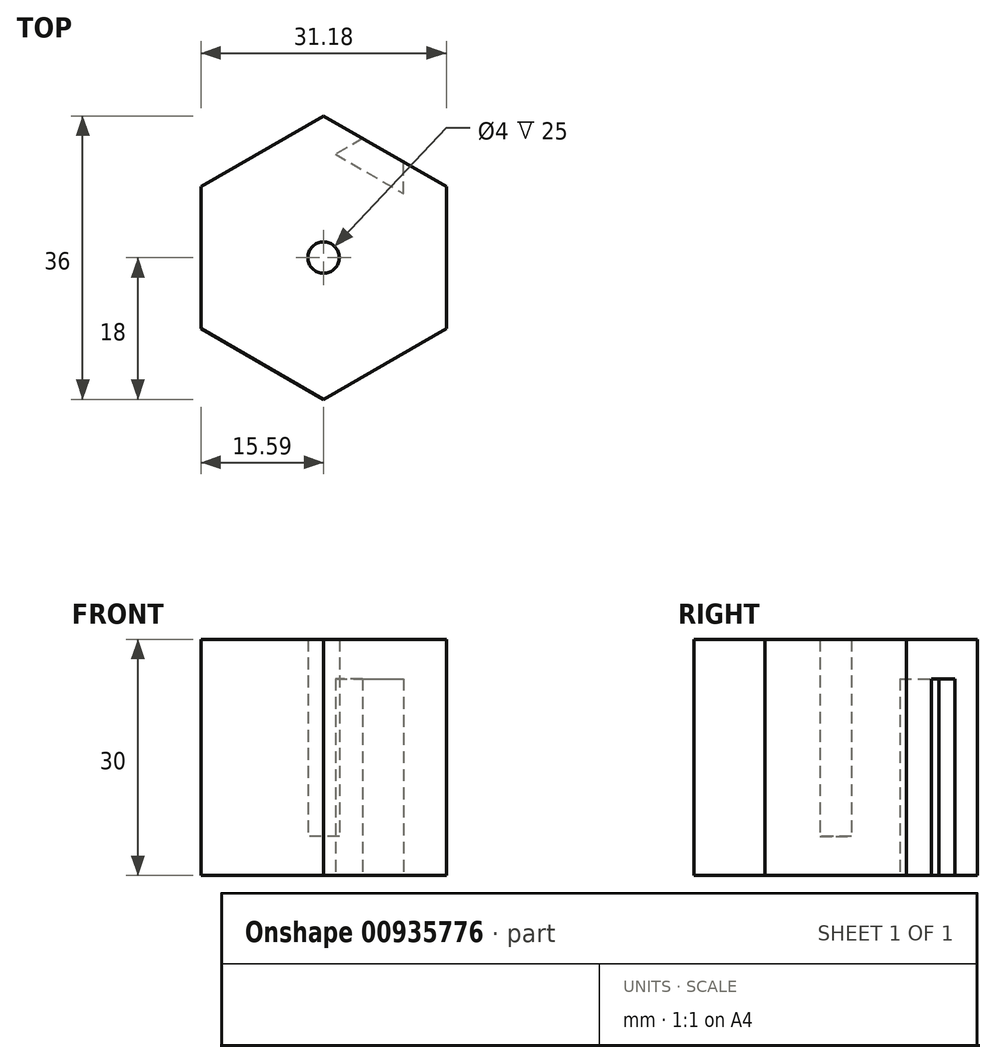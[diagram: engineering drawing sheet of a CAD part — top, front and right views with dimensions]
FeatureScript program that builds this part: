
annotation { "Feature Type Name" : "Feature", "Feature Type Description" : "" }
export const myFeature = defineFeature(function(context is Context, id is Id, definition is map)
    precondition{}
    {
        {
            var Q0;
            Q0=qCreatedBy(makeId("Top.planeOp"),FACE);
            var sketch = newSketch(context, id + "F0", { "sketchPlane" : qUnion([Q0])});
            skCircle(sketch, "E0.cCircle", {"center": v(0, 0) * mm, "radius": 18 * mm, "construction": true});
            skLineSegment(sketch, "E0.0", {"start": v(-15.59, 9) * mm, "end": v(0, 18) * mm});
            skLineSegment(sketch, "E0.1", {"start": v(0, 18) * mm, "end": v(15.59, 9) * mm});
            skLineSegment(sketch, "E0.2", {"start": v(15.59, 9) * mm, "end": v(15.59, -9) * mm});
            skLineSegment(sketch, "E0.3", {"start": v(15.59, -9) * mm, "end": v(0, -18) * mm});
            skLineSegment(sketch, "E0.4", {"start": v(0, -18) * mm, "end": v(-15.59, -9) * mm});
            skLineSegment(sketch, "E0.5", {"start": v(-15.59, -9) * mm, "end": v(-15.59, 9) * mm});
            skCircle(sketch, "E1", {"center": v(0, 0) * mm, "radius": 2 * mm});
            skLineSegment(sketch, "E2", {"start": v(4.96, 15.14) * mm, "end": v(1.5, 13.14) * mm});
            skLineSegment(sketch, "E3", {"start": v(1.5, 13.14) * mm, "end": v(10.15, 8.14) * mm});
            skLineSegment(sketch, "E4", {"start": v(10.15, 8.14) * mm, "end": v(10.15, 12.14) * mm});
            skLineSegment(sketch, "E5", {"start": v(10.15, 12.14) * mm, "end": v(4.96, 15.14) * mm});
            skSolve(sketch);
        }
        {
            var Q0;
            Q0=makeQuery(id+"F0.imprint","IMPRINT",FACE,{"disambiguationData":[TD([[makeQuery(id+"F0.imprint","IMPRINT",EDGE,{"derivedFrom":sQuery(id+"F0.wireOp",EDGE,"E1")}),1.0]])]});
            extrude(context, id + "F1", {"entities" : qUnion([Q0]), "depth" : 5 * mm, "offsetDistance" : 25 * mm});
        }
        {
            var Q0;
            Q0=makeQuery(id+"F0.imprint","IMPRINT",FACE,{"disambiguationData":[TD([[makeQuery(id+"F0.imprint","IMPRINT",EDGE,{"derivedFrom":sQuery(id+"F0.wireOp",EDGE,"E0.0")}),-1.0]])]});
            extrude(context, id + "F2", {"entities" : qUnion([Q0]), "operationType" : NewBodyOperationType.ADD, "depth" : 30 * mm, "offsetDistance" : 25 * mm});
        }
        {
            var Q0;
            Q0=makeQuery(id+"F0.imprint","IMPRINT",FACE,{"disambiguationData":[TD([[makeQuery(id+"F0.imprint","IMPRINT",EDGE,{"derivedFrom":sQuery(id+"F0.wireOp",EDGE,"E2")}),1.0]])]});
            extrude(context, id + "F3", {"entities" : qUnion([Q0]), "operationType" : NewBodyOperationType.ADD, "depth" : 30 * mm, "offsetDistance" : 25 * mm, "hasSecondDirection" : true, "secondDirectionOppositeDirection" : true, "secondDirectionDepth" : -25 * mm});
        }
    });
